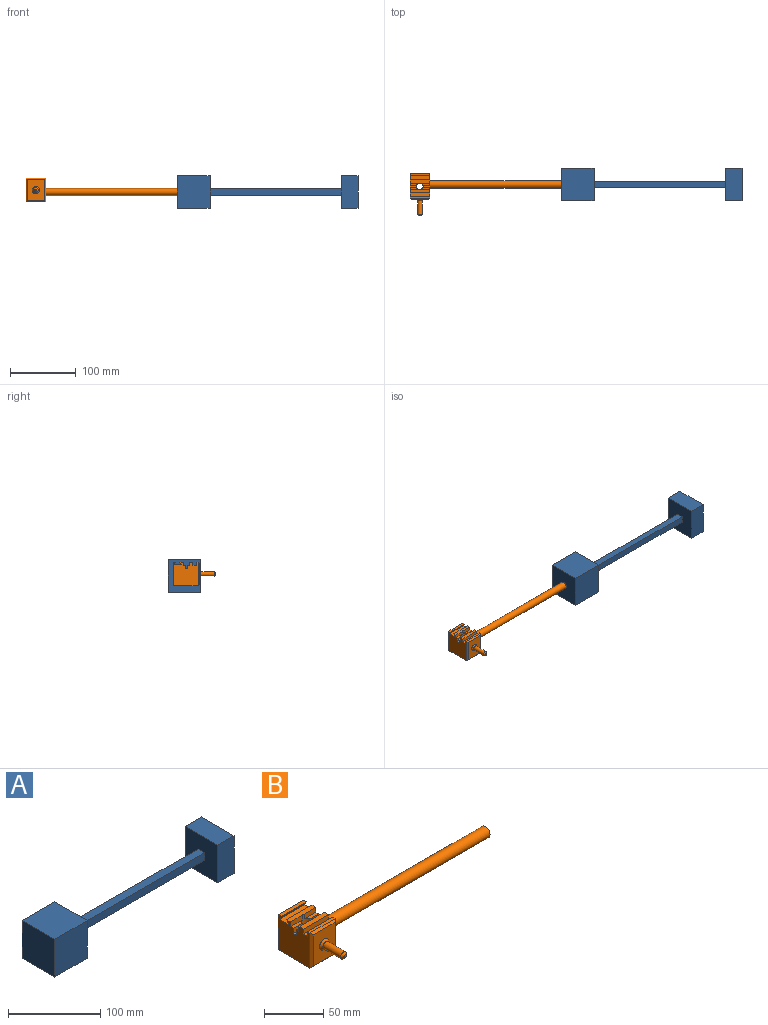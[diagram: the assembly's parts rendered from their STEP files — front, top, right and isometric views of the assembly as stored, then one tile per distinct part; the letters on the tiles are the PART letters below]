
ASSEMBLY  parts=2 mates=1
PART A: 16 faces, bbox 275x50x50 mm
  f0: plane 50x50mm, normal (-1,0,0), area 2500mm2, adj f1,f3,f4,f5
  f1: plane 50x50mm, normal (0,-1,0), area 2500mm2, adj f0,f2,f4,f5
  f2: plane 50x50mm, normal (1,0,0), area 2400mm2, adj f1,f3,f4,f5,f6,f7,f8,f9
  f3: plane 50x50mm, normal (0,1,0), area 2500mm2, adj f0,f2,f4,f5
  f4: plane 50x50mm, normal (0,0,1), area 2500mm2, adj f0,f1,f2,f3
  f5: plane 50x50mm, normal (0,0,-1), area 2500mm2, adj f0,f1,f2,f3
  f6: plane 200x10mm, normal (0,0,-1), area 2000mm2, adj f2,f7,f9,f15
  f7: plane 200x10mm, normal (0,1,0), area 2000mm2, adj f2,f6,f8,f15
  f8: plane 200x10mm, normal (0,0,1), area 2000mm2, adj f2,f7,f9,f15
  f9: plane 200x10mm, normal (0,-1,0), area 2000mm2, adj f2,f6,f8,f15
  f10: plane 50x25mm, normal (0,0,-1), area 1250mm2, adj f11,f13,f14,f15
  f11: plane 50x25mm, normal (0,1,0), area 1250mm2, adj f10,f12,f14,f15
  f12: plane 50x25mm, normal (0,0,1), area 1250mm2, adj f11,f13,f14,f15
  f13: plane 50x25mm, normal (0,-1,0), area 1250mm2, adj f10,f12,f14,f15
  f14: plane 50x50mm, normal (1,0,0), area 2500mm2, adj f10,f11,f12,f13
  f15: plane 50x50mm, normal (-1,0,0), area 2400mm2, adj f6,f7,f8,f9,f10,f11,f12,f13
PART B: 40 faces, bbox 230x65x36.1 mm
  f0: plane 30x3.75mm, normal (0,0,1), area 112.5mm2, adj f2,f5,f7,f28
  f1: cylinder r=5.12mm len=36.07mm, axis (0,0,-1), area 990mm2, adj f3,f6,f9,f10,f11,f12,f13,f14
  f2: plane 38x36.07mm, normal (1,0,0), area 1154.6mm2, adj f0,f3,f4,f6,f7,f9,f10,f11
  f3: plane 30x5mm, normal (0,0,1), area 149.8mm2, adj f1,f2,f5,f16,f19,f23
  f4: plane 30x3mm, normal (0,0,1), area 90mm2, adj f2,f5,f17,f37
  f5: plane 38x36.07mm, normal (-1,0,0), area 1245.3mm2, adj f0,f3,f4,f6,f7,f9,f13,f14
  f6: plane 30x4.75mm, normal (0,0,1), area 142.3mm2, adj f1,f2,f5,f21,f25,f29
  f7: plane 36.07x30mm, normal (0,1,0), area 1082mm2, adj f0,f2,f5,f9
  f8: plane 32.07x26mm, normal (0,-1,0), area 738.7mm2, adj f33,f34,f35,f36,f37
  f9: plane 38x30mm, normal (0,0,-1), area 1057.8mm2, adj f1,f2,f5,f7,f34
  f10: plane 10.11x5mm, normal (0,-1,0), area 50.5mm2, adj f1,f2,f12,f26
  f11: plane 10.11x5mm, normal (0,1,0), area 50.5mm2, adj f1,f2,f12,f24
  f12: plane 10.11x3mm, normal (0,0,1), area 29.9mm2, adj f1,f2,f10,f11
  f13: plane 10.11x5mm, normal (0,-1,0), area 50.5mm2, adj f1,f5,f15,f22
  f14: plane 10.11x5mm, normal (0,1,0), area 50.5mm2, adj f1,f5,f15,f20
  f15: plane 10.11x3mm, normal (0,0,1), area 29.9mm2, adj f1,f5,f13,f14
  f16: plane 30x5mm, normal (0,-1,0), area 150mm2, adj f2,f3,f5,f18
  f17: plane 30x5mm, normal (0,1,0), area 150mm2, adj f2,f4,f5,f18
  f18: plane 30x5mm, normal (0,0,1), area 150mm2, adj f2,f5,f16,f17
  f19: plane 13.92x5mm, normal (0,1,0), area 69.6mm2, adj f1,f3,f5,f20
  f20: plane 13.92x3.5mm, normal (0,0,1), area 39.6mm2, adj f1,f5,f14,f19
  f21: plane 13.92x5mm, normal (0,-1,0), area 69.6mm2, adj f1,f5,f6,f22
  f22: plane 13.92x3.5mm, normal (0,0,1), area 39.6mm2, adj f1,f5,f13,f21
  f23: plane 13.92x5mm, normal (0,1,0), area 69.6mm2, adj f1,f2,f3,f24
  f24: plane 13.92x3.5mm, normal (0,0,1), area 39.6mm2, adj f1,f2,f11,f23
  f25: plane 13.92x5mm, normal (0,-1,0), area 69.6mm2, adj f1,f2,f6,f26
  f26: plane 13.92x3.5mm, normal (0,0,1), area 39.6mm2, adj f1,f2,f10,f25
  f27: plane 30x11.12mm, normal (0,0,1), area 333.6mm2, adj f2,f5,f28,f29
  f28: plane 30x4mm, normal (0,-0.87,-0.5), area 138.6mm2, adj f0,f2,f5,f27
  f29: plane 30x4mm, normal (0,0.87,-0.5), area 138.6mm2, adj f2,f5,f6,f27
  f30: cylinder r=3.5mm len=21mm, axis (0,1,0), area 461.8mm2, adj f32,f33
  f31: plane 3x3mm, normal (0,-1,0), area 7.1mm2, adj f32
  f32: cone r=1.5mm half-angle=45deg, axis (0,1,0), area 44.4mm2, adj f30,f31
  f33: cone r=3.5mm half-angle=45deg, axis (0,1,0), area 80mm2, adj f8,f30
  f34: plane 30x2mm, normal (0,-0.71,-0.71), area 79.2mm2, adj f8,f9,f35,f36
  f35: plane 36.07x2mm, normal (-0.71,-0.71,0), area 96.4mm2, adj f5,f8,f34,f37
  f36: plane 36.07x2mm, normal (0.71,-0.71,0), area 96.4mm2, adj f2,f8,f34,f37
  f37: plane 30x2mm, normal (0,-0.71,0.71), area 79.2mm2, adj f4,f8,f35,f36
  f38: cylinder r=5.37mm len=200mm, axis (-1,0,0), area 6752.8mm2, adj f2,f39
  f39: plane 10.75x10.75mm, normal (1,0,0), area 90.7mm2, adj f38
PLACE A t=(-24.24,-21.22,-21.82)mm
PLACE B t=(-143.19,0.86,-11.86)mm
MATE fastened B.f38 <-> A.f0  axis (1,0,0) through (-24.24,3.78,3.18)mm
